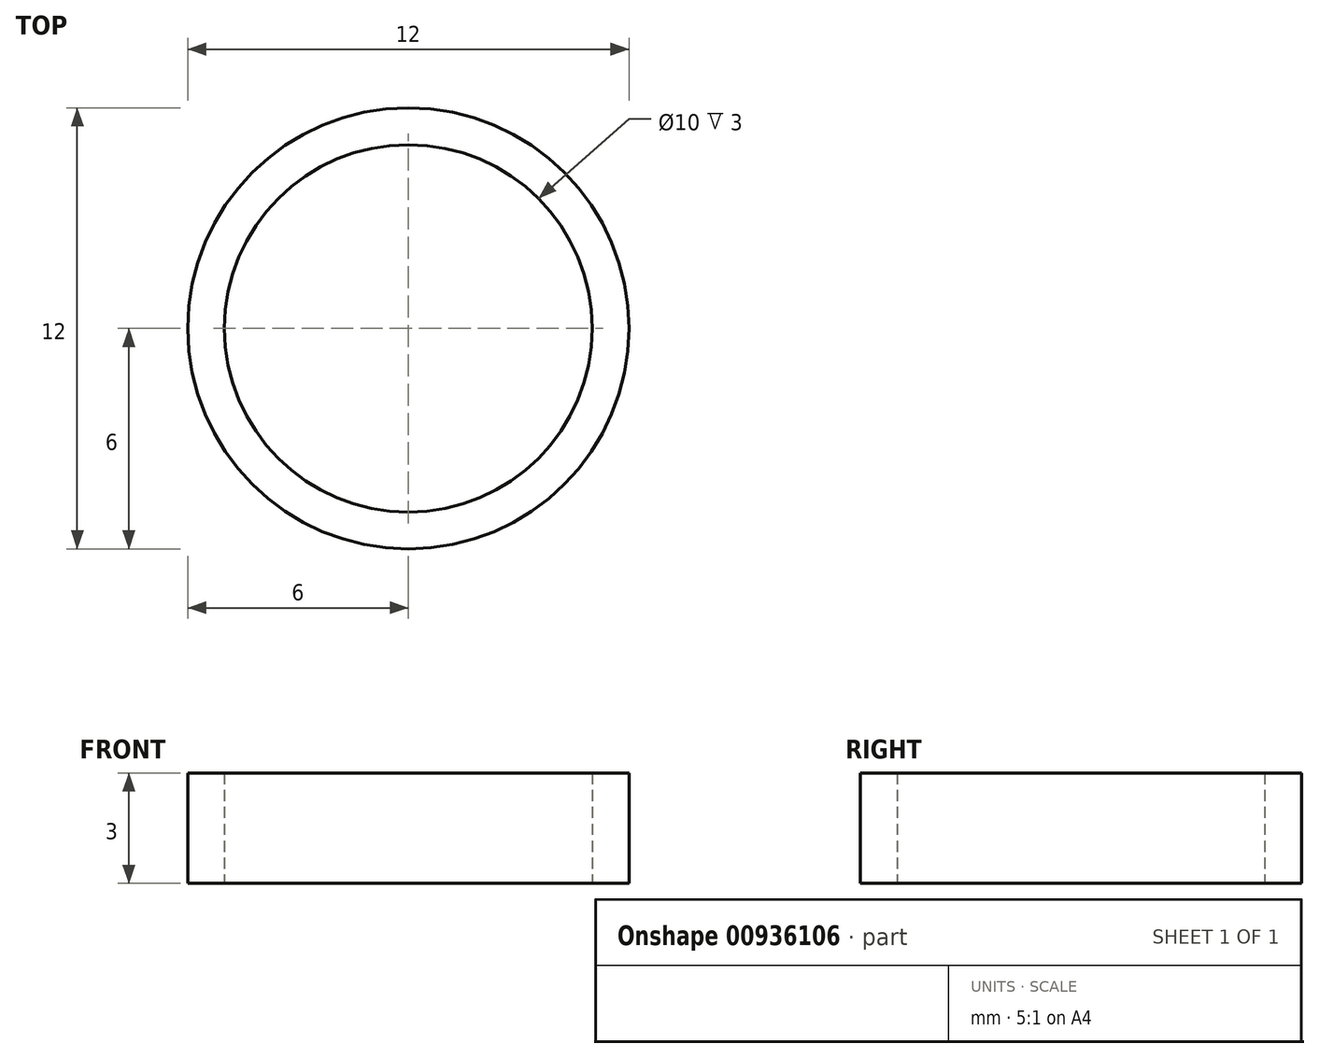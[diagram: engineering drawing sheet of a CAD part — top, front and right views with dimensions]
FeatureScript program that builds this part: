
annotation { "Feature Type Name" : "Feature", "Feature Type Description" : "" }
export const myFeature = defineFeature(function(context is Context, id is Id, definition is map)
    precondition{}
    {
        {
            var Q0;
            Q0=qCreatedBy(makeId("Top.planeOp"),FACE);
            var sketch = newSketch(context, id + "F0", { "sketchPlane" : qUnion([Q0])});
            skCircle(sketch, "E0", {"center": v(0, 0) * mm, "radius": 5 * mm});
            skCircle(sketch, "E1", {"center": v(0, 0) * mm, "radius": 6 * mm});
            skSolve(sketch);
        }
        {
            var Q0;
            Q0=makeQuery(id+"F0.imprint","IMPRINT",FACE,{"disambiguationData":[TD([[makeQuery(id+"F0.imprint","IMPRINT",EDGE,{"derivedFrom":sQuery(id+"F0.wireOp",EDGE,"E0")}),-1.0]])]});
            extrude(context, id + "F1", {"entities" : qUnion([Q0]), "depth" : 3 * mm, "offsetDistance" : 25 * mm});
        }
    });
